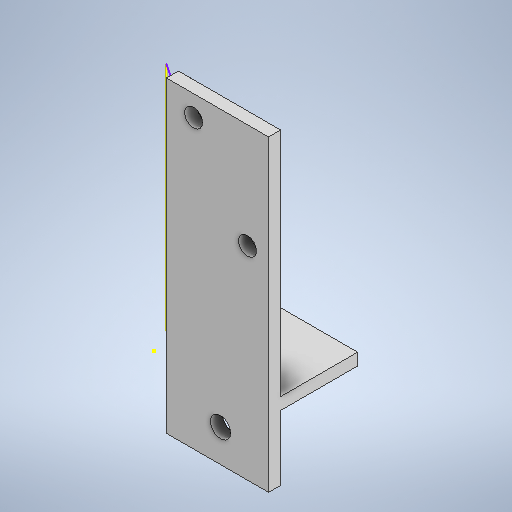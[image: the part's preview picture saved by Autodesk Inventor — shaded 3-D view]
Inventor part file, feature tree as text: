
AUTODESK INVENTOR PART (.ipt)
format: ipt  version: 2025.1 (Build 291241000, 241)  size: 305,664 bytes
history: native  units: in
note: dims shown in document units (in); Inventor stores cm internally (conversion verified against a paired STEP export)
features: extrude x7, sketch x6, move_body x4, direct_edit x2
ambient origin geometry x8: Origin, YZ Plane, XZ Plane, XY Plane, X Axis, Y Axis, Z Axis, Center Point
bodies: Solid1 (feature_tree)
feature tree (19):
  extrude  "Extrusion1"  Depth=0.8in
  extrude  "Extrusion2"  Depth=0.125in
  extrude  "Extrusion3"  Depth=0.125in
  extrude  "Extrusion4"  Depth=2.4in TaperAngle=0.0deg
  extrude  "Extrusion7"  Depth=1.8125in TaperAngle=0.0deg
  direct_edit  "Direct Edit1"
  direct_edit  "Direct Edit8"
  sketch  "Sketch16"  dims[d39=0.0in d40=0.0in d41=0.125in d76=0.395in d77=0.395in d78=1.55in d79=0.115in d80=0.115in d81=0.215in d82=0.46in d83=0.1875in d84=0.1875in d99=0.0in d100=0.0in d101=0.1875in d107=0.25in d108=0.0in d109=0.0in d110=0.0in d111=-0.0625in d112=0.125in d113=0.0in d114=0.0in d115=0.0in d116=-0.063in d42=0.0in]
  extrude  "Extrusion18"  Depth=0.125in
  extrude  "Extrusion19"  Depth=0.125in
  sketch  "Sketch1"  dims[d0=1.0in d1=0.8in]
  sketch  "Sketch2"  dims[d2=0.1245in d3=0.0in d4=0.125in]
  sketch  "Sketch3"  dims[d5=0.675in d6=0.0in d7=0.125in]
  sketch  "Sketch4"  dims[d8=2.4in d9=0.0in d16=2.5in d17=0.0in]
  sketch  "Sketch7"  dims[d23=0.21in d24=1.8125in d25=0.0in]
  move_body  "Move1"
  move_body  "Move11"
  move_body  "Move13"
  move_body  "Move14"
